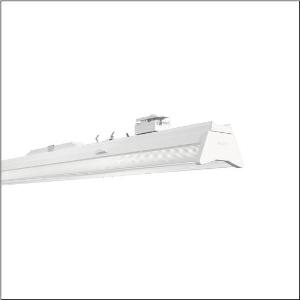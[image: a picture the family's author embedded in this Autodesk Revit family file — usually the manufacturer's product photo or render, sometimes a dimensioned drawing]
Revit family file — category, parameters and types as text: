
# Revit family: licross_r__21_performance_ho_52td16dn4e5m_0710
name_source: partatom
category: Lighting Fixtures
units: mm (PartAtom-declared; Revit-internal decimal feet)

## family parameters
Cut with Voids When Loaded = No
Host = Face
Light Source = No
Part Type = Normal
Room Calculation Point = No
Round Connector Dimension = Use Diameter
Shared = No

## types (1)
- --- (1 x LED, 14870 lm, 84.9 W, 4000K)
    Apparent Load = 85 VA
    CIE Flux Codes = 63 87 95 78 100
    Color Rendering = 80
    Color Temperature = 4000K
    Default Elevation = 1800 mm
    Description = Licross® 21 Performance HO, luminaire insert, of sheet steel, galvanised, coil coated, white, length: 1.500mm, width: 120mm, height: 123mm, LED rated luminous flux: 14.870lm, light colour: 840, control gear: DALI 2, with plug, 5-pole, with phase selection, mains connection: 220..240V, AC, 50/60Hz, rated input power: 85W, halogen-free wiring, primary light control with lens, of plastic, primary optical cover: cover, of PMMA, light emission: direct/indirect distribution, primary light characteristic: symmetric, protection rating (complete): IP54, insulation class (complete): insulation class I (protective earthing), certification: CE, ENEC, VDE, UKCA, protection symbol: D if used in an environment with non-conductive dust loads with corresponding accessories, impact resistance: IK06, permissible ambient temperature for indoor applications: -25..+35°C, corresponds to IFS (International Featured Standards) requirements for safety and quality in the food industry, reducing of maximum allowable ambient temperature of 5°C with ceiling mounting, LABS conformity tested according to VDMA 24364:2018-05, packaging unit: 1 piece
    Height = 114 mm
    Lamp = 1 x LED
    Lamp Light Flux = 14870 lm
    Lamp Power = 84.9 W
    Lamp count = 1
    Length = 1500 mm
    Luminous efficacy = 175 lm/W
    Manufacturer = Siteco
    ModVariant = No
    Model = 52TD16DN4E5M
    Mounting Place = Ceiling
    Mounting Type = Pendant
    Number of Poles = 1
    OnlyDefault = Yes
    Power Factor = 1
    Product Name = Licross® 21 Performance HO
    Product group = luminaire insert
    ProductGroupID = 901
    Protection Class = Protection class I
    Protection Degree = IP 54
    RLX_Detail_Level = 1
    RLX_Emergency_Light_Flux = 0 lm
    RLX_Emergency_Type = 0
    RLX_Emergency_Type_DB = No
    RlxData = <blob elided: 34025 chars, md5=98a8d395>
    Socket = socket
    Standby Power = 0 W
    System Light Flux = 14870 lm
    System Power = 85 W
    Type Comments = factory setting: luminous flux: 100 % | dim-lin: 254 | 484 mA
    Type Image = l_1256138.jpg
    URL = http://relux.com
    VarID = @adj_060917
    Voltage = 0 V
    Weight = 0.00 kg
    Width = 120 mm

## geometry (parser evidence)
native form markers: Blend x4, Sweep x14
no freeform markers — native parametric forms only
